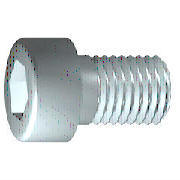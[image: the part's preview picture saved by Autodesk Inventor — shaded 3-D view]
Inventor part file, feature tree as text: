
AUTODESK INVENTOR PART (.ipt)
format: ipt  version: 2020 (Build 240168000, 168)  size: 202,240 bytes
history: native  units: mm (DEFAULTED — no unit token found)
features: sketch x2, extrude x1, plane x1, fillet x1
ambient origin geometry x7: Origin, YZ Plane, XY Plane, X Axis, Y Axis, Z Axis, Center Point
bodies: Solid1 (feature_tree), Body (feature_tree)
feature tree (5):
  extrude  "Slot"  Depth=2.0mm
  plane  "Work Plane1"
  fillet  "Fillet2"  Radius=2.0mm
  sketch  "Sketch1"  dims[d1=3.5mm d2=0.306825mm d3=2.0mm]
  sketch  "Sketch2"  dims[d4=1.5mm d5=60.0deg d6=3.0mm d7=3.0mm d8=2.309401mm d9=5.5mm d10=90.0deg d11=10.0mm d12=0.0mm d13=3.5mm d14=0.0mm d15=0.306725mm d16=0.306725mm d17=0.3mm d19=0.0mm d26=5.0mm d27=45.0deg d28=0.0mm d29=0.0mm d30=0.1mm]
